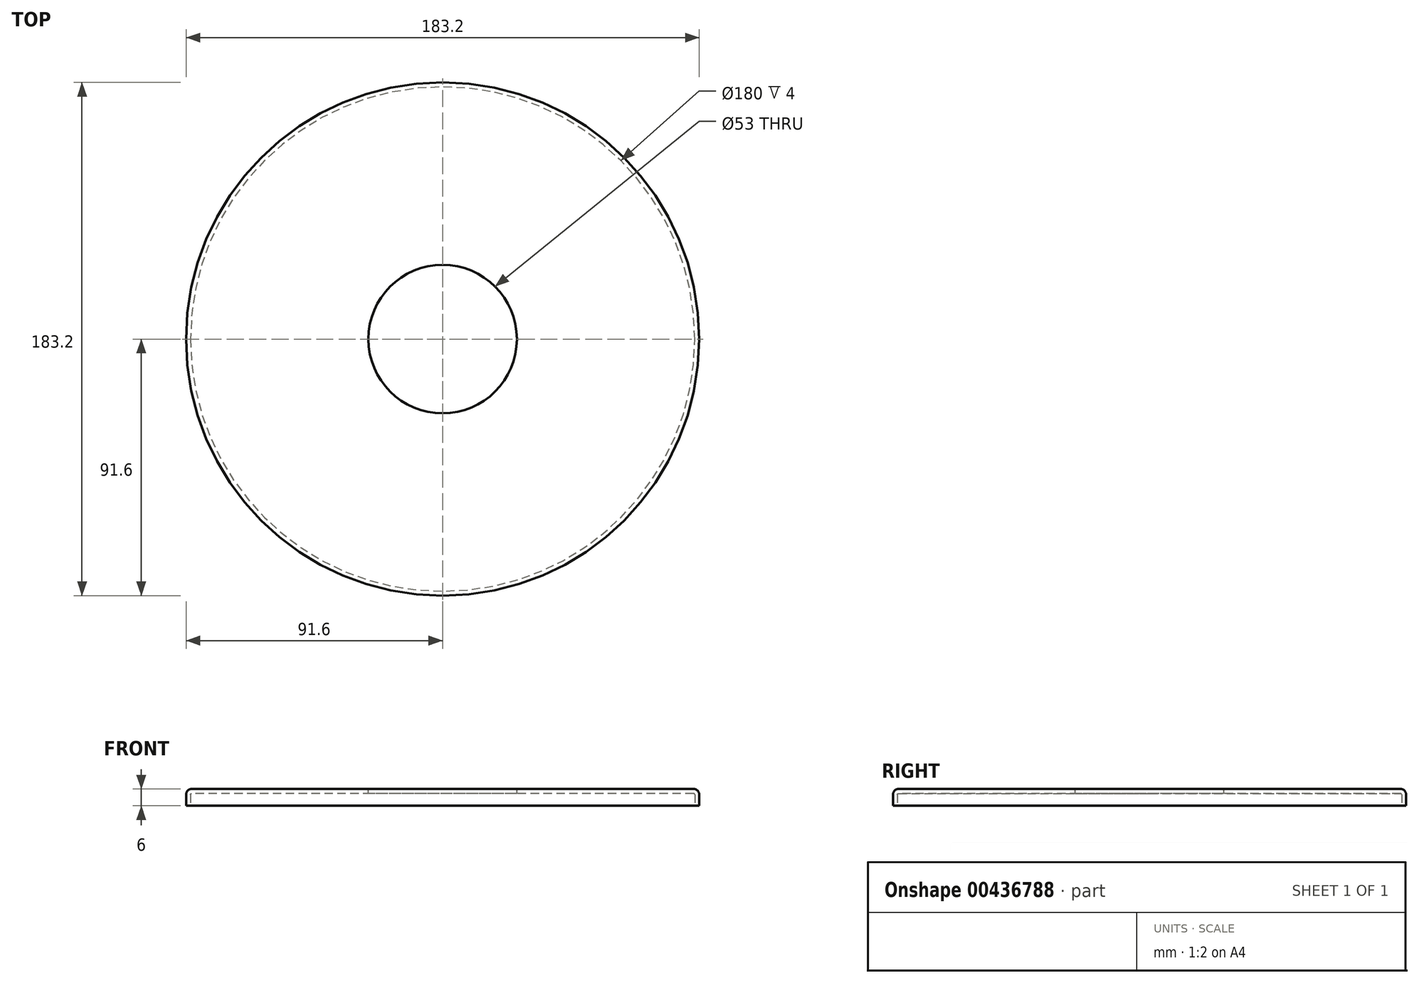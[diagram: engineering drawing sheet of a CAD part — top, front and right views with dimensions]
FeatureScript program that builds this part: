
annotation { "Feature Type Name" : "Feature", "Feature Type Description" : "" }
export const myFeature = defineFeature(function(context is Context, id is Id, definition is map)
    precondition{}
    {
        {
            var Q0;
            Q0=qCreatedBy(makeId("Top.planeOp"),FACE);
            var sketch = newSketch(context, id + "F0", { "sketchPlane" : qUnion([Q0])});
            skCircle(sketch, "E0", {"center": v(0, 0) * mm, "radius": 91.6 * mm});
            skSolve(sketch);
        }
        {
            var Q0;
            Q0 = qSketchRegion(id + "F0", true);
            extrude(context, id + "F1", {"entities" : qUnion([Q0]), "depth" : 6 * mm});
        }
        {
            var Q0;
            Q0=makeQuery(id+"F1.opExtrude","CAP_EDGE",EDGE,{"disambiguationData":[OSD([sQuery(id+"F0.wireOp",EDGE,"E0")])],"isStart":false});
            fillet(context, id + "F2", {"entities" : qUnion([Q0]), "radius" : 2 * mm, "tangentPropagation" : true, "allowEdgeOverflow" : false});
        }
        {
            var Q0;
            Q0=makeQuery(id+"F1.opExtrude","CAP_FACE",FACE,{"disambiguationData":[OSD([sQuery(id+"F0.wireOp",EDGE,"E0")])],"isStart":true});
            shell(context, id + "F3", {"entities" : qUnion([Q0]), "thickness" : 1.6 * mm});
        }
        {
            var Q0;
            Q0=makeQuery(id+"F1.opExtrude","CAP_FACE",FACE,{"disambiguationData":[OSD([sQuery(id+"F0.wireOp",EDGE,"E0")])],"isStart":false});
            var sketch = newSketch(context, id + "F4", { "sketchPlane" : qUnion([Q0])});
            skPoint(sketch, "E1", {"position": v(0, 0) * mm});
            skSolve(sketch);
        }
        {
            var Q0;
            Q0=makeQuery(id+"F1.opExtrude","SWEPT_BODY",BODY,{"disambiguationData":[OSD([sQuery(id+"F0.wireOp",EDGE,"E0")])]});
            transform(context, id + "F5", {"entities" : qUnion([Q0]), "transformType" : TransformType.TRANSLATION_3D, "dx" : 0 * mm, "dy" : 0 * mm, "dz" : 0 * mm, "makeCopy" : true});
        }
        {
            var Q0;
            {var subQ0=sQuery(id+"F0.wireOp",EDGE,"E0");Q0=makeQuery(id+"F4.imprint","IMPRINT",FACE,{"disambiguationData":[TD([[makeQuery(id+"F4.imprint","IMPRINT",EDGE,{"derivedFrom":makeQuery(id+"F2.opFillet","BLEND_EDGE",EDGE,{"blendedFrom":[makeQuery(id+"F1.opExtrude","CAP_EDGE",EDGE,{"disambiguationData":[OSD([subQ0])],"isStart":false}),makeQuery(id+"F1.opExtrude","CAP_FACE",FACE,{"disambiguationData":[OSD([subQ0])],"isStart":false})],"blendedInto":[makeQuery(id+"F1.opExtrude","CAP_FACE",FACE,{"disambiguationData":[OSD([subQ0])],"isStart":false})]})}),1.0]])]});}
            var sketch = newSketch(context, id + "F6", { "sketchPlane" : qUnion([Q0])});
            skCircle(sketch, "E2", {"center": v(0, 0) * mm, "radius": 30 * mm});
            skSolve(sketch);
        }
        {
            var Q0;
            Q0 = qSketchRegion(id + "F6", true);
            extrude(context, id + "F7", {"entities" : qUnion([Q0]), "depth" : 50 * mm});
        }
        {
            var Q0;
            Q0=makeQuery(id+"F7.opExtrude","CAP_FACE",FACE,{"disambiguationData":[OSD([sQuery(id+"F6.wireOp",EDGE,"E2")])],"isStart":false});
            var sketch = newSketch(context, id + "F8", { "sketchPlane" : qUnion([Q0])});
            skCircle(sketch, "E3", {"center": v(0, 0) * mm, "radius": 26.5 * mm});
            skSolve(sketch);
        }
        {
            var Q0;
            Q0=makeQuery(id+"F8.imprint","IMPRINT",FACE,{"disambiguationData":[TD([[makeQuery(id+"F8.imprint","IMPRINT",EDGE,{"derivedFrom":sQuery(id+"F8.wireOp",EDGE,"E3")}),1.0]])]});
            extrude(context, id + "F9", {"entities" : qUnion([Q0]), "operationType" : NewBodyOperationType.REMOVE, "endBound" : BoundingType.THROUGH_ALL, "oppositeDirection" : true, "depth" : 25 * mm});
        }
        {
            var Q0;
            Q0=makeQuery(id+"F5.opPattern","COPY",BODY,{"derivedFrom":makeQuery(id+"F1.opExtrude","SWEPT_BODY",BODY,{"disambiguationData":[OSD([sQuery(id+"F0.wireOp",EDGE,"E0")])]}),"instanceName":"1"});
            deleteBodies(context, id + "F10", {"entities" : qUnion([Q0])});
        }
        {
            var Q0;
            Q0=makeQuery(id+"F7.opExtrude","SWEPT_BODY",BODY,{"disambiguationData":[OSD([sQuery(id+"F6.wireOp",EDGE,"E2")])]});
            deleteBodies(context, id + "F11", {"entities" : qUnion([Q0])});
        }
        {
            var Q0;
            Q0=sQuery(id+"F4.wireOp",VERTEX,"E1");
            var Q1;
            Q1=makeQuery(id+"F1.opExtrude","SWEPT_BODY",BODY,{"disambiguationData":[OSD([sQuery(id+"F0.wireOp",EDGE,"E0")])]});
            hole(context, id + "F12", {"style" : HoleStyle.SIMPLE, "endStyle" : HoleEndStyle.THROUGH, "standardTappedOrClearance" : lookupTablePath({ "standard" : "ISO", "fit" : "Normal", "size" : "M8", "type" : "Clearance" }), "standardBlindInLast" : lookupTablePath({ "fit" : "Standard", "standard" : "ISO", "size" : "M8", "type" : "Clearance" }), "holeDiameter" : 8.8 * mm, "isTappedThrough" : true, "tappedDepth" : 12 * mm, "tapClearance" : 3, "locations" : qUnion([Q0]), "scope" : qUnion([Q1])});
        }
    });
